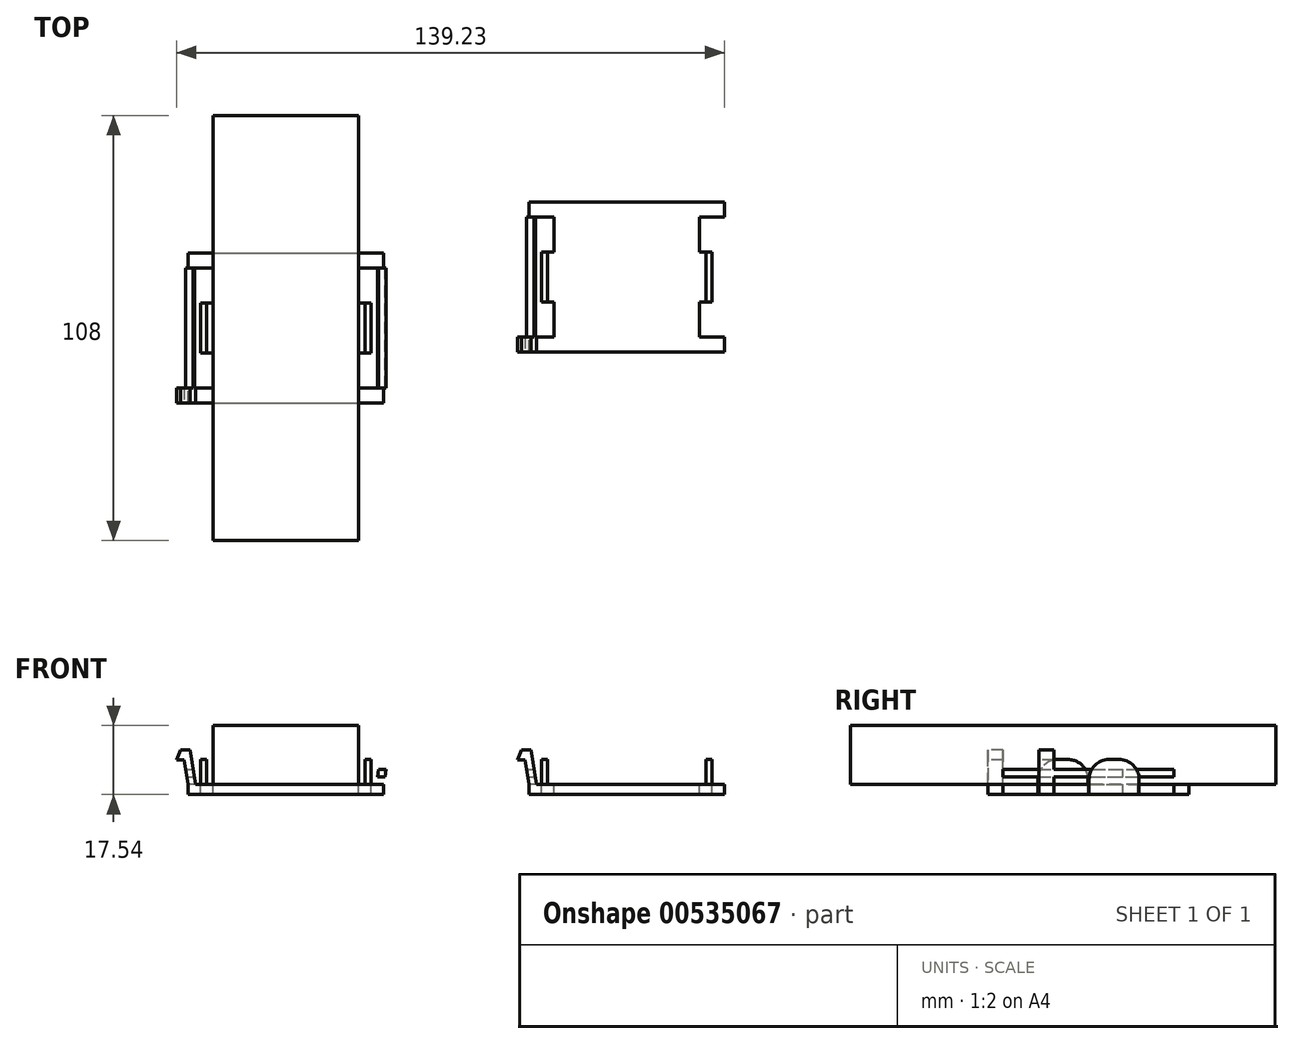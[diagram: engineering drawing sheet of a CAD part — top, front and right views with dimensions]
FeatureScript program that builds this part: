
annotation { "Feature Type Name" : "Feature", "Feature Type Description" : "" }
export const myFeature = defineFeature(function(context is Context, id is Id, definition is map)
    precondition{}
    {
        {
            var Q0;
            Q0=qCreatedBy(makeId("Top.planeOp"),FACE);
            var sketch = newSketch(context, id + "F0", { "sketchPlane" : qUnion([Q0])});
            skLineSegment(sketch, "E0.bottom", {"start": v(18.5, -54) * mm, "end": v(-18.5, -54) * mm});
            skLineSegment(sketch, "E0.top", {"start": v(18.5, 54) * mm, "end": v(-18.5, 54) * mm});
            skLineSegment(sketch, "E0.left", {"start": v(18.5, -54) * mm, "end": v(18.5, 54) * mm});
            skLineSegment(sketch, "E0.right", {"start": v(-18.5, -54) * mm, "end": v(-18.5, 54) * mm});
            skPoint(sketch, "E0.middle", {"position": v(0, 0) * mm});
            skSolve(sketch);
        }
        {
            var Q0;
            Q0 = qSketchRegion(id + "F0", true);
            extrude(context, id + "F1", {"entities" : qUnion([Q0]), "depth" : 15 * mm, "offsetDistance" : 25.4 * mm});
        }
        {
            var Q0;
            Q0=qCreatedBy(makeId("Top.planeOp"),FACE);
            var sketch = newSketch(context, id + "F2", { "sketchPlane" : qUnion([Q0])});
            skPoint(sketch, "E1.0", {"position": v(-18.5, 0) * mm});
            skPoint(sketch, "E2.0", {"position": v(0, -54) * mm});
            skLineSegment(sketch, "E3.bottom", {"start": v(18.5, -19.05) * mm, "end": v(-18.5, -19.05) * mm});
            skLineSegment(sketch, "E3.top", {"start": v(18.5, 19.05) * mm, "end": v(-18.5, 19.05) * mm});
            skLineSegment(sketch, "E3.left", {"start": v(18.5, -19.05) * mm, "end": v(18.5, 19.05) * mm});
            skLineSegment(sketch, "E3.right", {"start": v(-18.5, -19.05) * mm, "end": v(-18.5, 19.05) * mm});
            skPoint(sketch, "E3.middle", {"position": v(0, 0) * mm});
            skLineSegment(sketch, "E4.bottom", {"start": v(-18.5, -19.05) * mm, "end": v(-24.85, -19.05) * mm});
            skLineSegment(sketch, "E4.top", {"start": v(-18.5, -15.24) * mm, "end": v(-24.85, -15.24) * mm});
            skLineSegment(sketch, "E4.left", {"start": v(-18.5, -19.05) * mm, "end": v(-18.5, -15.24) * mm});
            skLineSegment(sketch, "E4.right", {"start": v(-24.85, -19.05) * mm, "end": v(-24.85, -15.24) * mm});
            skLineSegment(sketch, "E5", {"start": v(0, 0) * mm, "end": v(0, -10.12) * mm});
            skLineSegment(sketch, "E6", {"start": v(0, 0) * mm, "end": v(9.64, 0) * mm});
            skLineSegment(sketch, "E7.MirrorCS", {"start": v(-18.5, 19.05) * mm, "end": v(-24.85, 19.05) * mm});
            skLineSegment(sketch, "E8.MirrorCS", {"start": v(-18.5, 15.24) * mm, "end": v(-24.85, 15.24) * mm});
            skLineSegment(sketch, "E9.MirrorCS", {"start": v(-18.5, 19.05) * mm, "end": v(-18.5, 15.24) * mm});
            skLineSegment(sketch, "E10.MirrorCS", {"start": v(-24.85, 19.05) * mm, "end": v(-24.85, 15.24) * mm});
            skLineSegment(sketch, "E11.MirrorCS", {"start": v(18.5, 19.05) * mm, "end": v(18.5, 15.24) * mm});
            skLineSegment(sketch, "E12.MirrorCS", {"start": v(18.5, 15.24) * mm, "end": v(24.85, 15.24) * mm});
            skLineSegment(sketch, "E13.MirrorCS", {"start": v(18.5, 19.05) * mm, "end": v(24.85, 19.05) * mm});
            skLineSegment(sketch, "E14.MirrorCS", {"start": v(24.85, 19.05) * mm, "end": v(24.85, 15.24) * mm});
            skLineSegment(sketch, "E15.MirrorCS", {"start": v(24.85, -19.05) * mm, "end": v(24.85, -15.24) * mm});
            skLineSegment(sketch, "E16.MirrorCS", {"start": v(18.5, -19.05) * mm, "end": v(18.5, -15.24) * mm});
            skLineSegment(sketch, "E17.MirrorCS", {"start": v(18.5, -15.24) * mm, "end": v(24.85, -15.24) * mm});
            skLineSegment(sketch, "E18.MirrorCS", {"start": v(18.5, -19.05) * mm, "end": v(24.85, -19.05) * mm});
            skPoint(sketch, "E19.MirrorP", {"position": v(18.5, 0) * mm});
            skLineSegment(sketch, "E20.bottom", {"start": v(-21.68, -6.35) * mm, "end": v(-15.32, -6.35) * mm});
            skLineSegment(sketch, "E20.top", {"start": v(-21.68, 6.35) * mm, "end": v(-15.32, 6.35) * mm});
            skLineSegment(sketch, "E20.left", {"start": v(-21.68, -6.35) * mm, "end": v(-21.68, 6.35) * mm});
            skLineSegment(sketch, "E20.right", {"start": v(-15.32, -6.35) * mm, "end": v(-15.32, 6.35) * mm});
            skLineSegment(sketch, "E21.MirrorCS", {"start": v(15.32, -6.35) * mm, "end": v(15.32, 6.35) * mm});
            skLineSegment(sketch, "E22.MirrorCS", {"start": v(21.68, 6.35) * mm, "end": v(15.32, 6.35) * mm});
            skLineSegment(sketch, "E23.MirrorCS", {"start": v(21.68, -6.35) * mm, "end": v(21.68, 6.35) * mm});
            skLineSegment(sketch, "E24.MirrorCS", {"start": v(21.68, -6.35) * mm, "end": v(15.32, -6.35) * mm});
            skSolve(sketch);
        }
        {
            var Q0;
            Q0 = qSketchRegion(id + "F2", true);
            extrude(context, id + "F3", {"entities" : qUnion([Q0]), "oppositeDirection" : true, "depth" : 2.54 * mm, "offsetDistance" : 25.4 * mm});
        }
        {
            var Q0;
            Q0=makeQuery(id+"F3.opExtrude","CAP_FACE",FACE,{"disambiguationData":[OSD([sQuery(id+"F2.wireOp",EDGE,"E3.bottom"),sQuery(id+"F2.wireOp",EDGE,"E3.top"),sQuery(id+"F2.wireOp",EDGE,"E3.right"),sQuery(id+"F2.wireOp",EDGE,"E4.bottom"),sQuery(id+"F2.wireOp",EDGE,"E4.top"),sQuery(id+"F2.wireOp",EDGE,"E4.right"),sQuery(id+"F2.wireOp",EDGE,"E7.MirrorCS"),sQuery(id+"F2.wireOp",EDGE,"E8.MirrorCS"),sQuery(id+"F2.wireOp",EDGE,"E10.MirrorCS"),sQuery(id+"F2.wireOp",EDGE,"E12.MirrorCS"),sQuery(id+"F2.wireOp",EDGE,"E13.MirrorCS"),sQuery(id+"F2.wireOp",EDGE,"E14.MirrorCS"),sQuery(id+"F2.wireOp",EDGE,"E15.MirrorCS"),sQuery(id+"F2.wireOp",EDGE,"E17.MirrorCS"),sQuery(id+"F2.wireOp",EDGE,"E18.MirrorCS"),sQuery(id+"F2.wireOp",EDGE,"E3.left"),sQuery(id+"F2.wireOp",EDGE,"E20.bottom"),sQuery(id+"F2.wireOp",EDGE,"E20.top"),sQuery(id+"F2.wireOp",EDGE,"E20.left"),sQuery(id+"F2.wireOp",EDGE,"E22.MirrorCS"),sQuery(id+"F2.wireOp",EDGE,"E23.MirrorCS"),sQuery(id+"F2.wireOp",EDGE,"E24.MirrorCS")])],"isStart":true});
            var sketch = newSketch(context, id + "F4", { "sketchPlane" : qUnion([Q0])});
            skLineSegment(sketch, "E25.bottom", {"start": v(-21.68, 6.35) * mm, "end": v(-20.09, 6.35) * mm});
            skLineSegment(sketch, "E25.top", {"start": v(-21.68, -6.35) * mm, "end": v(-20.09, -6.35) * mm});
            skLineSegment(sketch, "E25.left", {"start": v(-21.68, 6.35) * mm, "end": v(-21.68, -6.35) * mm});
            skLineSegment(sketch, "E25.right", {"start": v(-20.09, 6.35) * mm, "end": v(-20.09, -6.35) * mm});
            skLineSegment(sketch, "E26.bottom", {"start": v(21.68, 6.35) * mm, "end": v(20.09, 6.35) * mm});
            skLineSegment(sketch, "E26.top", {"start": v(21.68, -6.35) * mm, "end": v(20.09, -6.35) * mm});
            skLineSegment(sketch, "E26.left", {"start": v(21.68, 6.35) * mm, "end": v(21.68, -6.35) * mm});
            skLineSegment(sketch, "E26.right", {"start": v(20.09, 6.35) * mm, "end": v(20.09, -6.35) * mm});
            skSolve(sketch);
        }
        {
            var Q0;
            Q0 = qSketchRegion(id + "F4", true);
            extrude(context, id + "F5", {"entities" : qUnion([Q0]), "operationType" : NewBodyOperationType.ADD, "depth" : 6.35 * mm, "offsetDistance" : 25.4 * mm});
        }
        {
            var Q0;
            Q0=makeQuery(id+"F5.opExtrude","CAP_EDGE",EDGE,{"disambiguationData":[OSD([sQuery(id+"F4.wireOp",EDGE,"E25.top")])],"isStart":false});
            var Q1;
            Q1=makeQuery(id+"F5.opExtrude","CAP_EDGE",EDGE,{"disambiguationData":[OSD([sQuery(id+"F4.wireOp",EDGE,"E25.bottom")])],"isStart":false});
            var Q2;
            Q2=makeQuery(id+"F5.opExtrude","CAP_EDGE",EDGE,{"disambiguationData":[OSD([sQuery(id+"F4.wireOp",EDGE,"E26.top")])],"isStart":false});
            var Q3;
            Q3=makeQuery(id+"F5.opExtrude","CAP_EDGE",EDGE,{"disambiguationData":[OSD([sQuery(id+"F4.wireOp",EDGE,"E26.bottom")])],"isStart":false});
            fillet(context, id + "F6", {"entities" : qUnion([Q0, Q1, Q2, Q3]), "radius" : 5.08 * mm, "tangentPropagation" : true, "allowEdgeOverflow" : false});
        }
        {
            var Q0;
            Q0=makeQuery(id+"F3.opExtrude","SWEPT_FACE",FACE,{"disambiguationData":[OSD([sQuery(id+"F2.wireOp",EDGE,"E3.bottom"),sQuery(id+"F2.wireOp",EDGE,"E4.bottom"),sQuery(id+"F2.wireOp",EDGE,"E18.MirrorCS")])]});
            var sketch = newSketch(context, id + "F7", { "sketchPlane" : qUnion([Q0])});
            skLineSegment(sketch, "E27", {"start": v(-24.85, 0) * mm, "end": v(-25.87, 6.22) * mm});
            skLineSegment(sketch, "E28", {"start": v(-25.87, 6.22) * mm, "end": v(-27.77, 6.22) * mm});
            skLineSegment(sketch, "E29", {"start": v(-27.77, 6.22) * mm, "end": v(-26.75, 8.76) * mm});
            skLineSegment(sketch, "E30", {"start": v(-26.75, 8.76) * mm, "end": v(-24.35, 8.76) * mm});
            skLineSegment(sketch, "E31", {"start": v(-24.35, 8.76) * mm, "end": v(-22.92, 0) * mm});
            skLineSegment(sketch, "E32", {"start": v(-22.92, 0) * mm, "end": v(-24.85, 0) * mm});
            skSolve(sketch);
        }
        {
            var Q0;
            Q0 = qSketchRegion(id + "F7", true);
            extrude(context, id + "F8", {"entities" : qUnion([Q0]), "operationType" : NewBodyOperationType.ADD, "oppositeDirection" : true, "depth" : 3.8 * mm, "offsetDistance" : 25.4 * mm});
        }
        {
            var Q0;
            Q0=qCreatedBy(makeId("Front.planeOp"),FACE);
            var sketch = newSketch(context, id + "F9", { "sketchPlane" : qUnion([Q0])});
            skLineSegment(sketch, "E33.0", {"start": v(-24.85, 0) * mm, "end": v(-25.87, 6.22) * mm});
            skLineSegment(sketch, "E34.0", {"start": v(-24.35, 8.76) * mm, "end": v(-22.92, 0) * mm});
            skLineSegment(sketch, "E35", {"start": v(-25.47, 3.8) * mm, "end": v(-23.54, 3.8) * mm});
            skLineSegment(sketch, "E36", {"start": v(-25.16, 1.9) * mm, "end": v(-23.23, 1.9) * mm});
            skPoint(sketch, "E37.0", {"position": v(0, -2.54) * mm});
            skLineSegment(sketch, "E38", {"start": v(0, -2.54) * mm, "end": v(0, 10.1) * mm});
            skLineSegment(sketch, "E39.MirrorCS", {"start": v(25.16, 1.9) * mm, "end": v(23.23, 1.9) * mm});
            skLineSegment(sketch, "E40.MirrorCS", {"start": v(25.47, 3.8) * mm, "end": v(23.54, 3.8) * mm});
            skLineSegment(sketch, "E41.MirrorCS", {"start": v(24.35, 8.76) * mm, "end": v(22.92, 0) * mm});
            skLineSegment(sketch, "E42.MirrorCS", {"start": v(24.85, 0) * mm, "end": v(25.87, 6.22) * mm});
            skSolve(sketch);
        }
        {
            var Q0;
            Q0 = qSketchRegion(id + "F9", true);
            extrude(context, id + "F10", {"entities" : qUnion([Q0]), "operationType" : NewBodyOperationType.ADD, "depth" : 30.48 * mm, "offsetDistance" : 25.4 * mm, "symmetric" : true});
        }
        {
            var Q0;
            Q0=makeQuery(id+"F3.opExtrude","SWEPT_BODY",BODY,{"disambiguationData":[OSD([sQuery(id+"F2.wireOp",EDGE,"E3.bottom"),sQuery(id+"F2.wireOp",EDGE,"E3.top"),sQuery(id+"F2.wireOp",EDGE,"E3.right"),sQuery(id+"F2.wireOp",EDGE,"E4.bottom"),sQuery(id+"F2.wireOp",EDGE,"E4.top"),sQuery(id+"F2.wireOp",EDGE,"E4.right"),sQuery(id+"F2.wireOp",EDGE,"E7.MirrorCS"),sQuery(id+"F2.wireOp",EDGE,"E8.MirrorCS"),sQuery(id+"F2.wireOp",EDGE,"E10.MirrorCS"),sQuery(id+"F2.wireOp",EDGE,"E12.MirrorCS"),sQuery(id+"F2.wireOp",EDGE,"E13.MirrorCS"),sQuery(id+"F2.wireOp",EDGE,"E14.MirrorCS"),sQuery(id+"F2.wireOp",EDGE,"E15.MirrorCS"),sQuery(id+"F2.wireOp",EDGE,"E17.MirrorCS"),sQuery(id+"F2.wireOp",EDGE,"E18.MirrorCS"),sQuery(id+"F2.wireOp",EDGE,"E3.left"),sQuery(id+"F2.wireOp",EDGE,"E20.bottom"),sQuery(id+"F2.wireOp",EDGE,"E20.top"),sQuery(id+"F2.wireOp",EDGE,"E20.left"),sQuery(id+"F2.wireOp",EDGE,"E22.MirrorCS"),sQuery(id+"F2.wireOp",EDGE,"E23.MirrorCS"),sQuery(id+"F2.wireOp",EDGE,"E24.MirrorCS")])]});
            transform(context, id + "F11", {"entities" : qUnion([Q0]), "transformType" : TransformType.TRANSLATION_3D, "dx" : 86.61 * mm, "dy" : 12.95 * mm, "dz" : 0 * mm, "makeCopy" : true});
        }
    });
